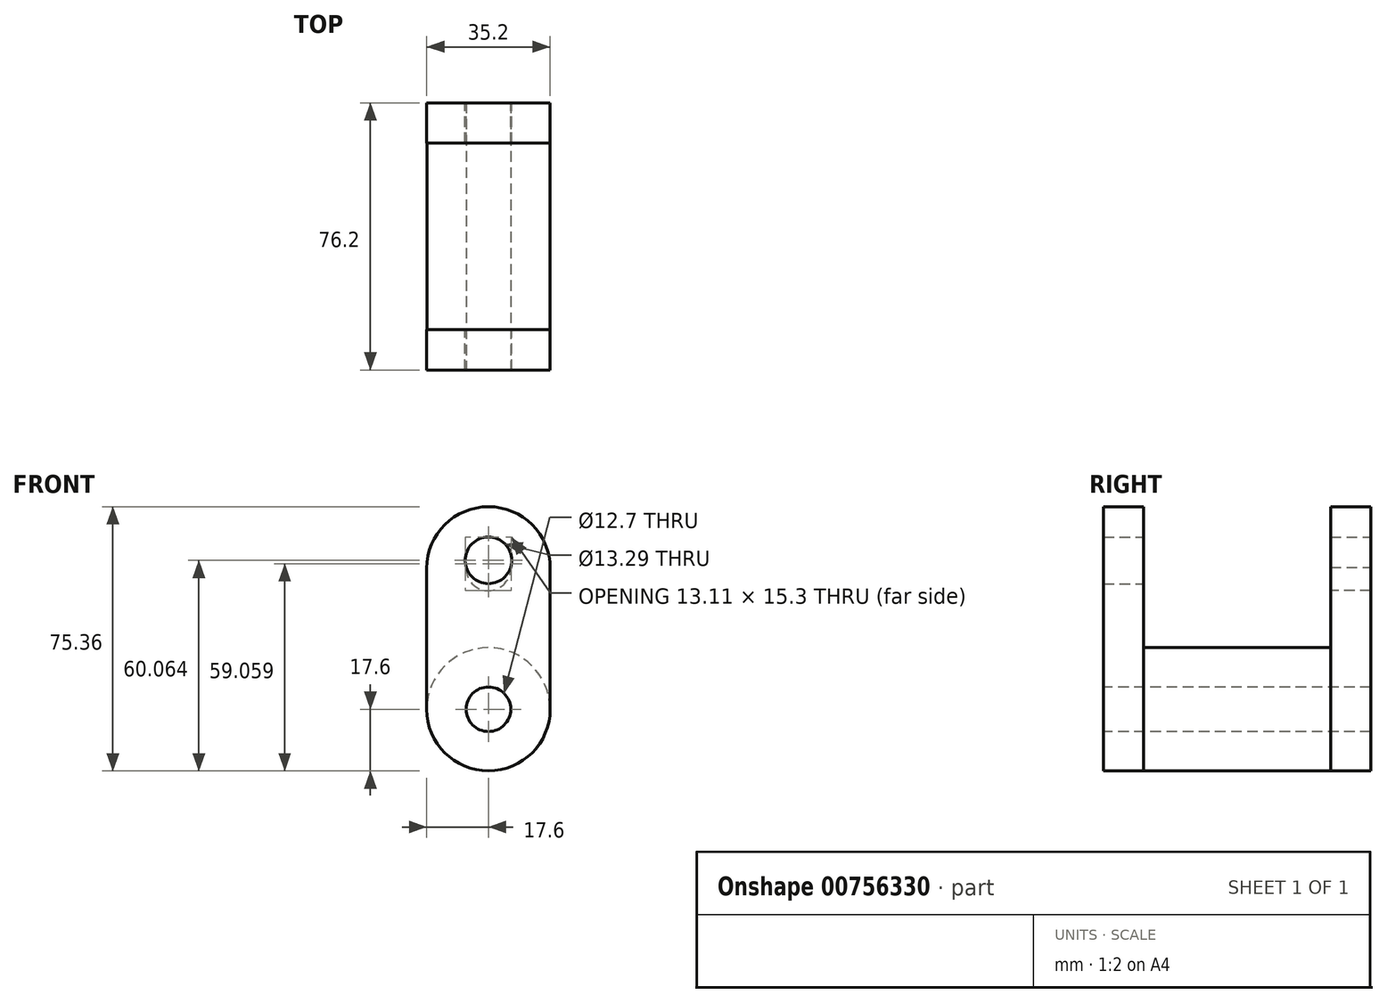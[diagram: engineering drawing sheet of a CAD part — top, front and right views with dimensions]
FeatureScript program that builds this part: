
annotation { "Feature Type Name" : "Feature", "Feature Type Description" : "" }
export const myFeature = defineFeature(function(context is Context, id is Id, definition is map)
    precondition{}
    {
        {
            var Q0;
            Q0=qCreatedBy(makeId("Front.planeOp"),FACE);
            var sketch = newSketch(context, id + "F0", { "sketchPlane" : qUnion([Q0])});
            skCircle(sketch, "E0", {"center": v(0, 0) * mm, "radius": 17.6 * mm});
            skLineSegment(sketch, "E1", {"start": v(-17.6, 0) * mm, "end": v(-17.6, 40.16) * mm});
            skLineSegment(sketch, "E2", {"start": v(17.6, 0) * mm, "end": v(17.6, 40.16) * mm});
            skCircle(sketch, "E3", {"center": v(0, 40.16) * mm, "radius": 17.6 * mm});
            skSolve(sketch);
        }
        {
            var Q0;
            {var subQ0=sQuery(id+"F0.wireOp",EDGE,"E3");var subQ1=makeQuery(id+"F0.imprint","INTERSECT",VERTEX,{"derivedFrom":[sQuery(id+"F0.wireOp",EDGE,"E1"),subQ0]});Q0=makeQuery(id+"F0.imprint","IMPRINT",FACE,{"disambiguationData":[TD([[makeQuery(id+"F0.imprint","IMPRINT",EDGE,{"disambiguationData":[TD([[subQ1,1.0]])],"derivedFrom":subQ0}),1.0]])]});}
            var Q1;
            {var subQ0=sQuery(id+"F0.wireOp",EDGE,"E0");var subQ1=makeQuery(id+"F0.imprint","INTERSECT",VERTEX,{"derivedFrom":[subQ0,sQuery(id+"F0.wireOp",EDGE,"E1")]});Q1=makeQuery(id+"F0.imprint","IMPRINT",FACE,{"disambiguationData":[TD([[makeQuery(id+"F0.imprint","IMPRINT",EDGE,{"disambiguationData":[TD([[subQ1,1.0]])],"derivedFrom":subQ0}),1.0]])]});}
            var Q2;
            {var subQ0=sQuery(id+"F0.wireOp",EDGE,"E1");Q2=makeQuery(id+"F0.imprint","IMPRINT",FACE,{"disambiguationData":[TD([[makeQuery(id+"F0.imprint","IMPRINT",EDGE,{"derivedFrom":subQ0}),-1.0]])]});}
            extrude(context, id + "F1", {"entities" : qUnion([Q0, Q1, Q2]), "oppositeDirection" : true, "depth" : 76.2 * mm, "offsetDistance" : 25.4 * mm, "symmetric" : true});
        }
        {
            var Q0;
            Q0=makeQuery(id+"F1.opExtrude","SWEPT_FACE",FACE,{"disambiguationData":[OSD([sQuery(id+"F0.wireOp",EDGE,"E2")])]});
            var sketch = newSketch(context, id + "F2", { "sketchPlane" : qUnion([Q0])});
            skLineSegment(sketch, "E4", {"start": v(-26.62, 66.93) * mm, "end": v(-26.62, -26.92) * mm});
            skLineSegment(sketch, "E5", {"start": v(-26.62, -26.92) * mm, "end": v(0, -26.92) * mm});
            skLineSegment(sketch, "E6", {"start": v(-26.62, 66.93) * mm, "end": v(0, 66.93) * mm});
            skLineSegment(sketch, "E7.MirrorCS", {"start": v(26.62, 66.93) * mm, "end": v(0, 66.93) * mm});
            skLineSegment(sketch, "E8.MirrorCS", {"start": v(26.62, 66.93) * mm, "end": v(26.62, -26.92) * mm});
            skLineSegment(sketch, "E9.MirrorCS", {"start": v(26.62, -26.92) * mm, "end": v(0, -26.92) * mm});
            skSolve(sketch);
        }
        {
            var Q0;
            {var subQ6=sQuery(id+"F2.wireOp",EDGE,"E6");Q0=makeQuery(id+"F2.imprint","IMPRINT",FACE,{"disambiguationData":[TD([[makeQuery(id+"F2.imprint","IMPRINT",EDGE,{"derivedFrom":subQ6}),-1.0]])]});}
            var Q1;
            {var subQ0=sQuery(id+"F2.wireOp",EDGE,"E4");var subQ1=sQuery(id+"F0.wireOp",EDGE,"E2");var subQ2=makeQuery(id+"F1.opExtrude","SWEPT_EDGE",EDGE,{"disambiguationData":[OSD([subQ1,sQuery(id+"F0.wireOp",EDGE,"E3")])]});var subQ3=makeQuery(id+"F2.imprint","INTERSECT",VERTEX,{"derivedFrom":[subQ2,subQ0]});Q1=makeQuery(id+"F2.imprint","IMPRINT",FACE,{"disambiguationData":[TD([[makeQuery(id+"F2.imprint","IMPRINT",EDGE,{"disambiguationData":[TD([[subQ3,-1.0]])],"derivedFrom":subQ0}),1.0]])]});}
            var Q2;
            {var subQ4=sQuery(id+"F2.wireOp",EDGE,"E5");Q2=makeQuery(id+"F2.imprint","IMPRINT",FACE,{"disambiguationData":[TD([[makeQuery(id+"F2.imprint","IMPRINT",EDGE,{"derivedFrom":subQ4}),1.0]])]});}
            extrude(context, id + "F3", {"entities" : qUnion([Q0, Q1, Q2]), "operationType" : NewBodyOperationType.REMOVE, "oppositeDirection" : true, "depth" : 50.8 * mm, "offsetDistance" : 25.4 * mm});
        }
        {
            var Q0;
            Q0=qCreatedBy(makeId("Front.planeOp"),FACE);
            var sketch = newSketch(context, id + "F4", { "sketchPlane" : qUnion([Q0])});
            skCircle(sketch, "E10", {"center": v(0, 0) * mm, "radius": 17.55 * mm});
            skSolve(sketch);
        }
        {
            var Q0;
            Q0 = qSketchRegion(id + "F4", true);
            extrude(context, id + "F5", {"entities" : qUnion([Q0]), "operationType" : NewBodyOperationType.ADD, "depth" : 76.2 * mm, "offsetDistance" : 25.4 * mm, "symmetric" : true});
        }
        {
            var Q0;
            Q0=sQuery(id+"F0.wireOp",VERTEX,"E3.center");
            var Q1;
            Q1=sQuery(id+"F0.wireOp",VERTEX,"E0.center");
            var Q2;
            Q2=makeQuery(id+"F5.opExtrude","SWEPT_BODY",BODY,{"disambiguationData":[OSD([sQuery(id+"F4.wireOp",EDGE,"E10")])]});
            var Q3;
            Q3=makeQuery(id+"F3.boolean.opBoolean","SPLIT",BODY,{"disambiguationData":[OD(1.0)],"derivedFrom":makeQuery(id+"F1.opExtrude","SWEPT_BODY",BODY,{"disambiguationData":[OSD([sQuery(id+"F0.wireOp",EDGE,"E0"),sQuery(id+"F0.wireOp",EDGE,"E1"),sQuery(id+"F0.wireOp",EDGE,"E2"),sQuery(id+"F0.wireOp",EDGE,"E3")])]})});
            hole(context, id + "F6", {"style" : HoleStyle.SIMPLE, "endStyle" : HoleEndStyle.THROUGH, "holeDiameter" : 12.7 * mm, "majorDiameter" : 6.35 * mm, "isTappedThrough" : true, "tappedDepth" : 12.7 * mm, "tapClearance" : 3, "locations" : qUnion([Q0, Q1]), "scope" : qUnion([Q2, Q3])});
        }
        {
            var Q0;
            Q0=makeQuery(id+"F1.opExtrude","CAP_FACE",FACE,{"disambiguationData":[OSD([sQuery(id+"F0.wireOp",EDGE,"E0"),sQuery(id+"F0.wireOp",EDGE,"E1"),sQuery(id+"F0.wireOp",EDGE,"E2"),sQuery(id+"F0.wireOp",EDGE,"E3")])],"isStart":true});
            var sketch = newSketch(context, id + "F7", { "sketchPlane" : qUnion([Q0])});
            skSolve(sketch);
        }
        {
            var Q0;
            Q0=makeQuery(id+"F7.imprint","IMPRINT",FACE,{"disambiguationData":[TD([[makeQuery(id+"F7.imprint","IMPRINT",EDGE,{"derivedFrom":makeQuery(id+"F1.opExtrude","CAP_EDGE",EDGE,{"disambiguationData":[OSD([sQuery(id+"F0.wireOp",EDGE,"E0")])],"isStart":true})}),1.0]])]});
            var sketch = newSketch(context, id + "F8", { "sketchPlane" : qUnion([Q0])});
            skPoint(sketch, "E11", {"position": v(0, 0) * mm});
            skSolve(sketch);
        }
        {
            var Q0;
            Q0=sQuery(id+"F8.wireOp",VERTEX,"E11");
            var Q1;
            Q1=makeQuery(id+"F3.boolean.opBoolean","SPLIT",BODY,{"disambiguationData":[OD(0.0)],"derivedFrom":makeQuery(id+"F1.opExtrude","SWEPT_BODY",BODY,{"disambiguationData":[OSD([sQuery(id+"F0.wireOp",EDGE,"E0"),sQuery(id+"F0.wireOp",EDGE,"E1"),sQuery(id+"F0.wireOp",EDGE,"E2"),sQuery(id+"F0.wireOp",EDGE,"E3")])]})});
            hole(context, id + "F9", {"style" : HoleStyle.SIMPLE, "endStyle" : HoleEndStyle.THROUGH, "holeDiameter" : 12.7 * mm, "majorDiameter" : 6.35 * mm, "isTappedThrough" : true, "tappedDepth" : 12.7 * mm, "tapClearance" : 3, "locations" : qUnion([Q0]), "scope" : qUnion([Q1])});
        }
        {
            var Q0;
            Q0=makeQuery(id+"F1.opExtrude","CAP_FACE",FACE,{"disambiguationData":[OSD([sQuery(id+"F0.wireOp",EDGE,"E0"),sQuery(id+"F0.wireOp",EDGE,"E1"),sQuery(id+"F0.wireOp",EDGE,"E2"),sQuery(id+"F0.wireOp",EDGE,"E3")])],"isStart":false});
            var sketch = newSketch(context, id + "F10", { "sketchPlane" : qUnion([Q0])});
            skCircle(sketch, "E12", {"center": v(0, 42.46) * mm, "radius": 6.64 * mm});
            skSolve(sketch);
        }
        {
            var Q0;
            Q0=makeQuery(id+"F10.imprint","IMPRINT",FACE,{"disambiguationData":[TD([[makeQuery(id+"F10.imprint","IMPRINT",EDGE,{"derivedFrom":sQuery(id+"F10.wireOp",EDGE,"E12")}),1.0]])]});
            extrude(context, id + "F11", {"entities" : qUnion([Q0]), "operationType" : NewBodyOperationType.REMOVE, "oppositeDirection" : true, "depth" : 127 * mm, "offsetDistance" : 25.4 * mm});
        }
    });
